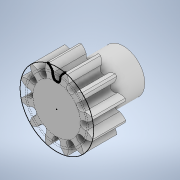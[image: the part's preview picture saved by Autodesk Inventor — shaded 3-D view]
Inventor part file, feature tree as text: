
AUTODESK INVENTOR PART (.ipt)
format: ipt  version: 2021 (Build 250183000, 183)  size: 252,928 bytes
history: native  units: in
note: dims shown in document units (in); Inventor stores cm internally (conversion verified against a paired STEP export)
features: extrude x3, sketch x2, pattern_circular x1
ambient origin geometry x8: Origin, YZ Plane, XZ Plane, XY Plane, X Axis, Y Axis, Z Axis, Center Point
bodies: Solid1 (feature_tree)
feature tree (6):
  sketch  "Sketch1"  dims[d0=0.25in d1=0.0in]
  extrude  "Extrusion1"  TaperAngle=0.0deg  [1 undecoded]
  extrude  "Extrusion2"  Depth=0.25in TaperAngle=360.0deg
  pattern_circular  "Circular Pattern1"  [2 undecoded]
  extrude  "Extrusion3"  Depth=0.25in
  sketch  "Sketch2"  dims[d2=0.0in d3=0.0in d4=4.7244in d5=360.0deg d7=0.1181in d8=0.1969in d9=0.0625in d10=0.25in d11=0.0in]
note: 3 required parameter values undecoded (feature->parameter linkage not recoverable at this tier; creation-order binding heuristic only, values carry confidence <= 0.55)
